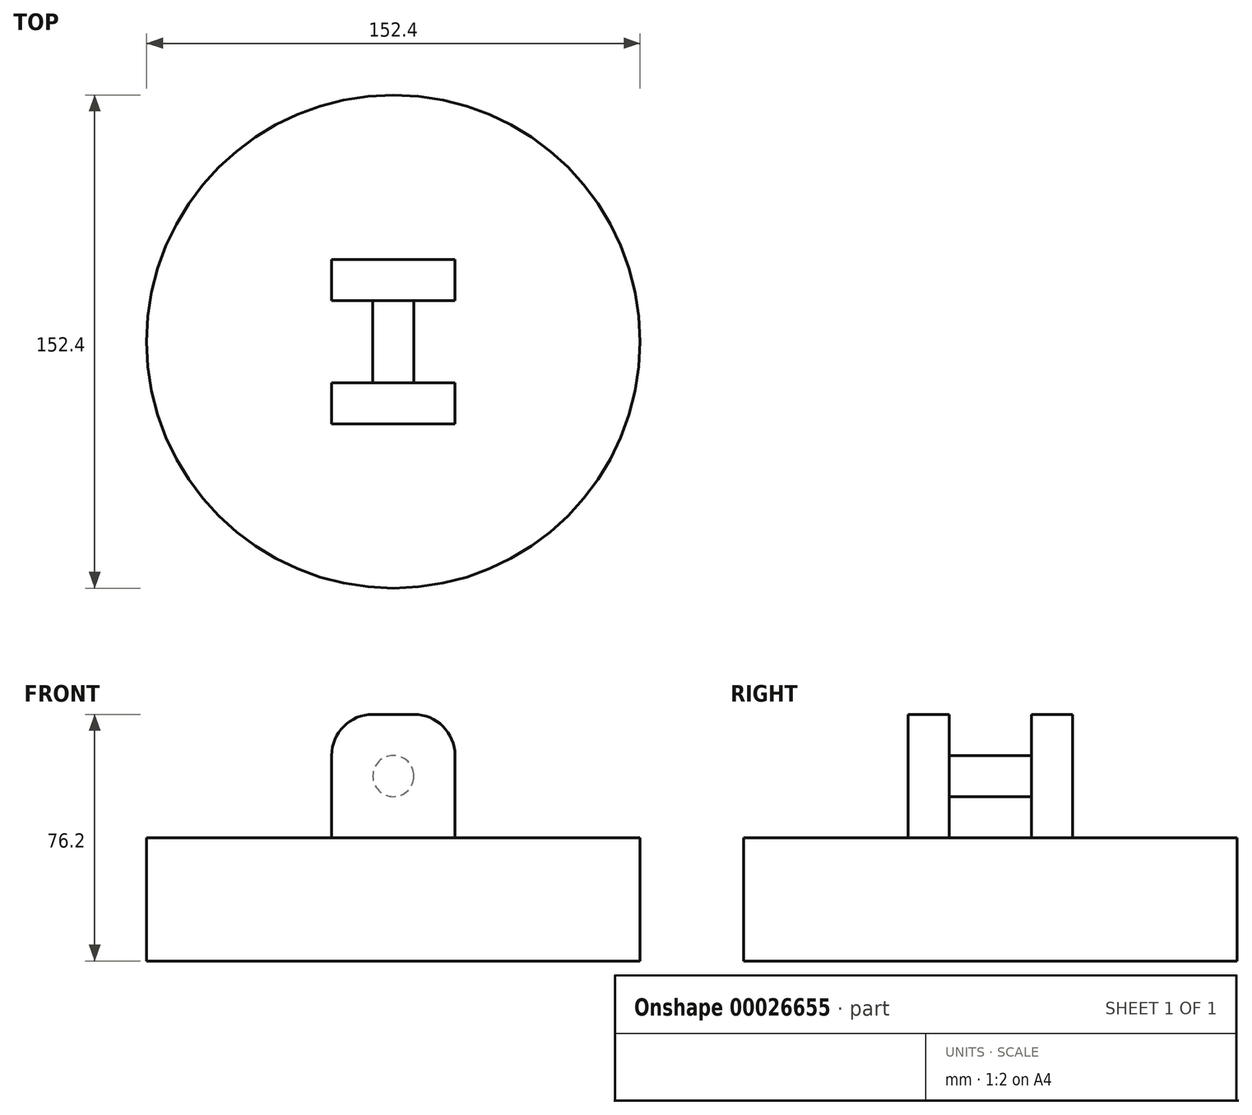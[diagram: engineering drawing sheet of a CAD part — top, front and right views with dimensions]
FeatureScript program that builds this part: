
annotation { "Feature Type Name" : "Feature", "Feature Type Description" : "" }
export const myFeature = defineFeature(function(context is Context, id is Id, definition is map)
    precondition{}
    {
        {
            var Q0;
            Q0=qCreatedBy(makeId("Top.planeOp"),FACE);
            var sketch = newSketch(context, id + "F0", { "sketchPlane" : qUnion([Q0])});
            skCircle(sketch, "E0", {"center": v(-36.06, 39.19) * mm, "radius": 76.2 * mm});
            skSolve(sketch);
        }
        {
            var Q0;
            Q0 = qSketchRegion(id + "F0", true);
            extrude(context, id + "F1", {"entities" : qUnion([Q0]), "depth" : 38.1 * mm});
        }
        {
            var Q0;
            Q0=makeQuery(id+"F1.opExtrude","CAP_FACE",FACE,{"disambiguationData":[OSD([sQuery(id+"F0.wireOp",EDGE,"E0")])],"isStart":false});
            var sketch = newSketch(context, id + "F2", { "sketchPlane" : qUnion([Q0])});
            skLineSegment(sketch, "E1.rect.bottom", {"start": v(-17, 13.79) * mm, "end": v(-55.1, 13.79) * mm});
            skLineSegment(sketch, "E1.rect.top", {"start": v(-17, 64.59) * mm, "end": v(-55.1, 64.59) * mm});
            skLineSegment(sketch, "E1.rect.left", {"start": v(-17, 13.79) * mm, "end": v(-17, 26.49) * mm});
            skLineSegment(sketch, "E1.rect.right", {"start": v(-55.1, 13.79) * mm, "end": v(-55.1, 26.49) * mm});
            skPoint(sketch, "E1.rect.middle", {"position": v(-36.06, 39.19) * mm});
            skLineSegment(sketch, "E2", {"start": v(-55.1, 51.89) * mm, "end": v(-17, 51.89) * mm});
            skLineSegment(sketch, "E3", {"start": v(-55.1, 26.49) * mm, "end": v(-17, 26.49) * mm});
            skLineSegment(sketch, "E4.trimOffspring", {"start": v(-55.1, 51.89) * mm, "end": v(-55.1, 64.59) * mm});
            skLineSegment(sketch, "E5.trimOffspring", {"start": v(-17, 51.89) * mm, "end": v(-17, 64.59) * mm});
            skSolve(sketch);
        }
        {
            var Q0;
            Q0=makeQuery(id+"F2.imprint","IMPRINT",FACE,{"disambiguationData":[TD([[makeQuery(id+"F2.imprint","IMPRINT",EDGE,{"derivedFrom":sQuery(id+"F2.wireOp",EDGE,"E1.rect.bottom")}),-1.0]])]});
            var Q1;
            Q1=makeQuery(id+"F2.imprint","IMPRINT",FACE,{"disambiguationData":[TD([[makeQuery(id+"F2.imprint","IMPRINT",EDGE,{"derivedFrom":sQuery(id+"F2.wireOp",EDGE,"E1.rect.top")}),1.0]])]});
            extrude(context, id + "F3", {"entities" : qUnion([Q0, Q1]), "operationType" : NewBodyOperationType.ADD, "depth" : 38.1 * mm});
        }
        {
            var Q0;
            Q0=makeQuery(id+"F3.opExtrude","SWEPT_FACE",FACE,{"disambiguationData":[OSD([sQuery(id+"F2.wireOp",EDGE,"E3")])]});
            var sketch = newSketch(context, id + "F4", { "sketchPlane" : qUnion([Q0])});
            skPoint(sketch, "E6.orphan", {"position": v(36.06, 76.2) * mm});
            skPoint(sketch, "E7.start.orphan", {"position": v(36.06, 38.1) * mm});
            skCircle(sketch, "E8", {"center": v(36.06, 57.15) * mm, "radius": 6.35 * mm});
            skSolve(sketch);
        }
        {
            var Q0;
            Q0=makeQuery(id+"F3.opExtrude","CAP_EDGE",EDGE,{"disambiguationData":[OSD([sQuery(id+"F2.wireOp",EDGE,"E1.rect.left")])],"isStart":false});
            var Q1;
            Q1=makeQuery(id+"F3.opExtrude","CAP_EDGE",EDGE,{"disambiguationData":[OSD([sQuery(id+"F2.wireOp",EDGE,"E1.rect.right")])],"isStart":false});
            var Q2;
            Q2=makeQuery(id+"F3.opExtrude","CAP_EDGE",EDGE,{"disambiguationData":[OSD([sQuery(id+"F2.wireOp",EDGE,"E5.trimOffspring")])],"isStart":false});
            var Q3;
            Q3=makeQuery(id+"F3.opExtrude","CAP_EDGE",EDGE,{"disambiguationData":[OSD([sQuery(id+"F2.wireOp",EDGE,"E4.trimOffspring")])],"isStart":false});
            fillet(context, id + "F5", {"entities" : qUnion([Q0, Q1, Q2, Q3]), "radius" : 12.7 * mm, "tangentPropagation" : true, "allowEdgeOverflow" : false});
        }
        {
            var Q0;
            Q0=makeQuery(id+"F4.imprint","IMPRINT",FACE,{"disambiguationData":[TD([[makeQuery(id+"F4.imprint","IMPRINT",EDGE,{"derivedFrom":sQuery(id+"F4.wireOp",EDGE,"E8")}),1.0]])]});
            extrude(context, id + "F6", {"entities" : qUnion([Q0]), "operationType" : NewBodyOperationType.ADD, "depth" : 25.4 * mm});
        }
    });
